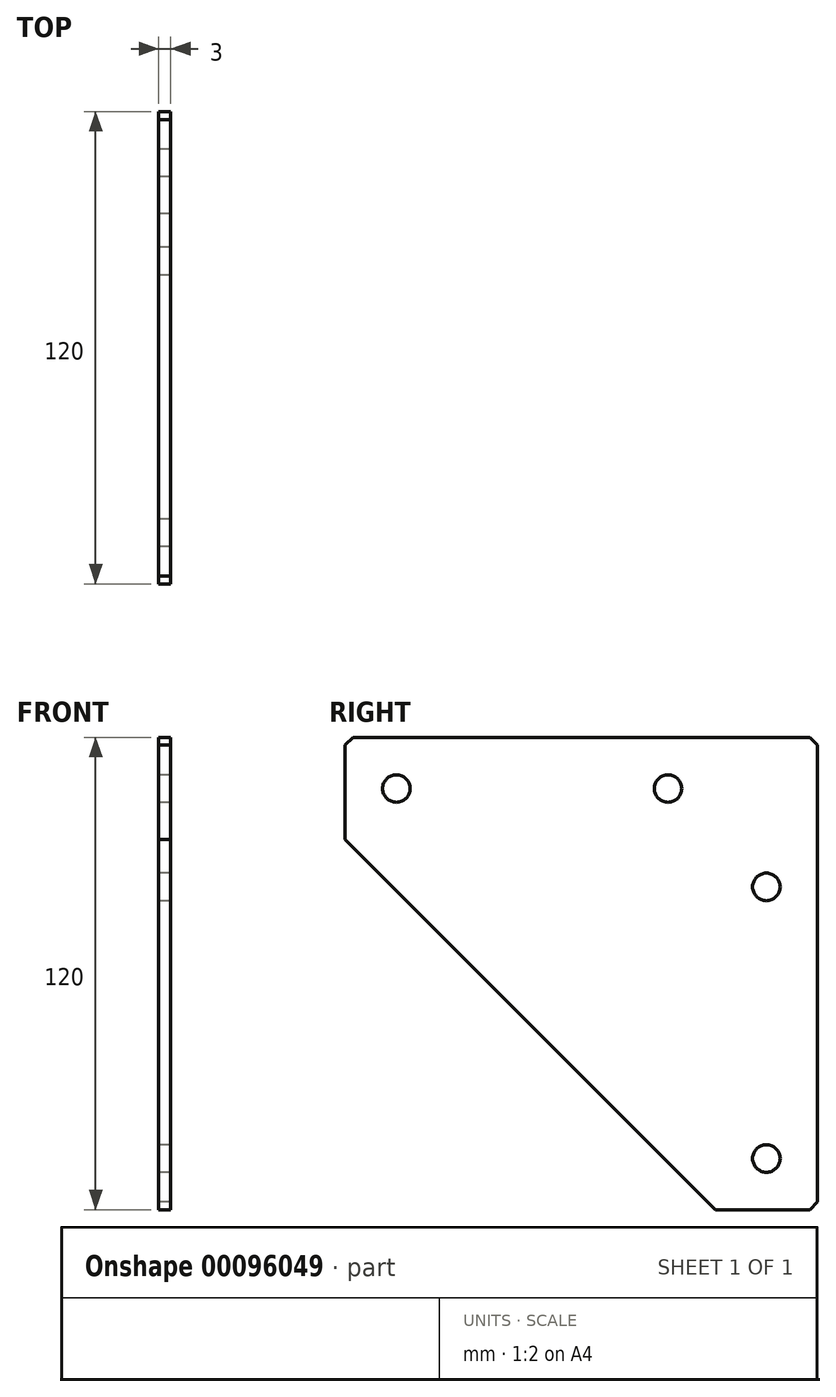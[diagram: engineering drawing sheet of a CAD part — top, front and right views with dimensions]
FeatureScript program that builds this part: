
annotation { "Feature Type Name" : "Feature", "Feature Type Description" : "" }
export const myFeature = defineFeature(function(context is Context, id is Id, definition is map)
    precondition{}
    {
        {
            var Q0;
            Q0=qCreatedBy(makeId("Right.planeOp"),FACE);
            var sketch = newSketch(context, id + "F0", { "sketchPlane" : qUnion([Q0])});
            skLineSegment(sketch, "E0", {"start": v(0, 0) * mm, "end": v(0, -120) * mm});
            skLineSegment(sketch, "E1", {"start": v(0, 0) * mm, "end": v(-120, 0) * mm});
            skLineSegment(sketch, "E2", {"start": v(0, -120) * mm, "end": v(-26, -120) * mm});
            skLineSegment(sketch, "E3", {"start": v(-120, 0) * mm, "end": v(-120, -26) * mm});
            skLineSegment(sketch, "E4", {"start": v(-26, -120) * mm, "end": v(-120, -26) * mm});
            skLineSegment(sketch, "E5", {"start": v(0, 0) * mm, "end": v(-73, -73) * mm});
            skCircle(sketch, "E6", {"center": v(-107, -13) * mm, "radius": 3.5 * mm});
            skCircle(sketch, "E7", {"center": v(-38, -13) * mm, "radius": 3.5 * mm});
            skCircle(sketch, "E8.MirrorC", {"center": v(-13, -38) * mm, "radius": 3.5 * mm});
            skCircle(sketch, "E9.MirrorC", {"center": v(-13, -107) * mm, "radius": 3.5 * mm});
            skSolve(sketch);
        }
        {
            var Q0;
            Q0=qSketchRegion(id+"F0",true);
            extrude(context, id + "F1", {"entities" : qUnion([Q0]), "endBound" : BoundingType.SYMMETRIC, "depth" : 3 * mm});
        }
        {
            var Q0;
            Q0=makeQuery(id+"F1.opExtrude","SWEPT_EDGE",EDGE,{"disambiguationData":[OSD([sQuery(id+"F0.wireOp",EDGE,"E1"),sQuery(id+"F0.wireOp",EDGE,"E3")])]});
            var Q1;
            Q1=makeQuery(id+"F1.opExtrude","SWEPT_EDGE",EDGE,{"disambiguationData":[OSD([sQuery(id+"F0.wireOp",EDGE,"E0"),sQuery(id+"F0.wireOp",EDGE,"E1"),sQuery(id+"F0.wireOp",EDGE,"E5")])]});
            var Q2;
            Q2=makeQuery(id+"F1.opExtrude","SWEPT_EDGE",EDGE,{"disambiguationData":[OSD([sQuery(id+"F0.wireOp",EDGE,"E0"),sQuery(id+"F0.wireOp",EDGE,"E2")])]});
            chamfer(context, id + "F2", {"entities" : qUnion([Q0, Q1, Q2]), "width" : 2 * mm, "tangentPropagation" : true});
        }
    });
